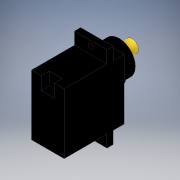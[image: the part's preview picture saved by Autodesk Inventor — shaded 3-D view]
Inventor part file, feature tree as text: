
AUTODESK INVENTOR PART (.ipt)
format: ipt  version: 2018 (Build 220112000, 112)  size: 198,144 bytes
history: native  units: mm
features: extrude x7, sketch x7, other x3
ambient origin geometry x8: Origin, YZ Plane, XZ Plane, XY Plane, X Axis, Y Axis, Z Axis, Center Point
bodies: Body1 (feature_tree)
feature tree (17):
  other  "Sólido1"
  extrude  "Extrusión1"  Depth=23.2mm
  extrude  "Extrusión2"  Depth=16.4mm
  other  "Edición directa1"
  extrude  "Extrusión3"  Depth=2.4mm
  extrude  "Extrusión4"  Depth=11.8mm TaperAngle=0.0deg
  extrude  "Extrusión5"  Depth=0.7mm
  extrude  "Extrusión6"  Depth=2.0mm
  extrude  "Extrusión8"  Depth=2.4mm TaperAngle=0.0deg
  sketch  "Boceto1"  dims[d0=11.8mm d1=23.2mm]
  sketch  "Boceto2"  dims[d2=23.0mm d3=0.0mm d4=16.4mm]
  sketch  "Boceto4"  dims[d5=4.7mm d6=2.4mm]
  sketch  "Boceto5"  dims[d7=4.7mm d8=11.8mm d9=0.0mm]
  sketch  "Boceto6"  dims[d10=0.0mm d11=0.0mm d12=0.7mm d13=1.9mm]
  sketch  "Boceto7"  dims[d14=1.9mm d15=2.0mm]
  sketch  "Boceto9"  dims[d16=2.0mm d17=2.4mm d18=0.0mm d19=15.0mm d20=4.3mm d21=0.0mm d22=5.0mm d23=4.8mm d24=5.0mm d25=0.0mm d26=6.25mm d28=4.3mm d29=0.0mm d35=3.0mm d36=2.5mm d37=5.0mm d38=0.0mm]
  other  "Desplazar1"
